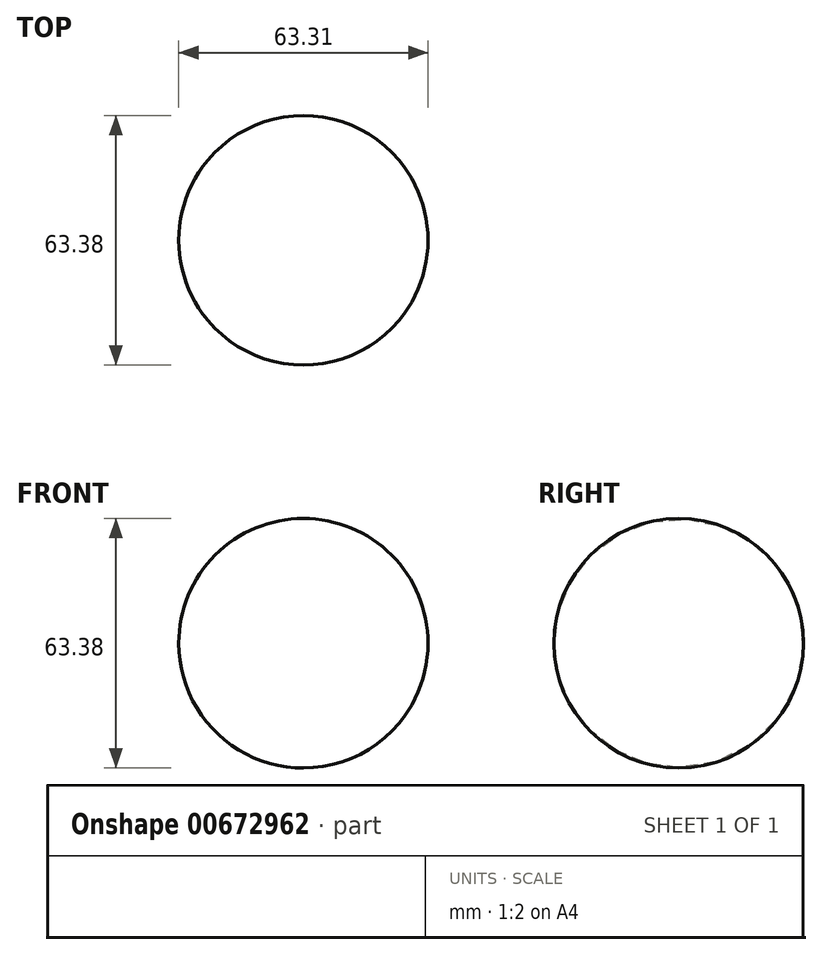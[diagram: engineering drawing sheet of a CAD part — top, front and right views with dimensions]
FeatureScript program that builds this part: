
annotation { "Feature Type Name" : "Feature", "Feature Type Description" : "" }
export const myFeature = defineFeature(function(context is Context, id is Id, definition is map)
    precondition{}
    {
        {
            var Q0;
            Q0=qCreatedBy(makeId("Front.planeOp"),FACE);
            var sketch = newSketch(context, id + "F0", { "sketchPlane" : qUnion([Q0])});
            skLineSegment(sketch, "E0", {"start": v(-31.51, 0) * mm, "end": v(31.8, 0) * mm});
            skArc(sketch, "E1", {"start": v(31.8, 0) * mm, "mid": v(0.14, 31.7) * mm, "end": v(-31.51, 0) * mm});
            skSolve(sketch);
        }
        {
            var Q0;
            Q0=makeQuery(id+"F0.imprint","IMPRINT",FACE,{"disambiguationData":[TD([[makeQuery(id+"F0.imprint","IMPRINT",EDGE,{"derivedFrom":sQuery(id+"F0.wireOp",EDGE,"E0")}),1.0]])]});
            var Q1;
            Q1=sQuery(id+"F0.wireOp",EDGE,"E0");
            revolve(context, id + "F1", {"entities" : qUnion([Q0]), "axis" : qUnion([Q1]), "revolveType" : RevolveType.FULL});
        }
    });
